MODEL slx_c33119aba72b
CONFIG AbsTol = auto
CONFIG EnableMultiTasking = off
CONFIG FixedStep = auto
CONFIG MaxStep = 1e-3
CONFIG MinStep = auto
CONFIG RelTol = 1e-3
CONFIG SampleTimeConstraint = Unconstrained
CONFIG SolverName = ode15s
CONFIG StartTime = 0.0
CONFIG StopTime = 10
BLOCK [Mux] Mux1
  DisplayOption = bar
  Inputs = 3
BLOCK [Reference] PID Controller  REF=slpidlib/PID Controller
  LibrarySourceBlock = simulink/Continuous/PID Controller
  SourceBlock = slpidlib/PID Controller
  SourceType = PID 1dof
BLOCK [Sin] Pa(t)
  Bias = 0.8
  Frequency = 2*pi*95/60
  SampleTime = 0
BLOCK [SubSystem] Pp(t): Caso [Hipotenso]
BLOCK [Gain] Pp(t): Caso [Hipotenso]/1//L
  Gain = 1/0.005
BLOCK [Gain] Pp(t): Caso [Hipotenso]/1//Z
  Gain = 1/0.02
BLOCK [Sum] Pp(t): Caso [Hipotenso]/Add
  IconShape = rectangular
  Inputs = ++-
BLOCK [Sum] Pp(t): Caso [Hipotenso]/Add1
  IconShape = rectangular
  Inputs = +-
BLOCK [Gain] Pp(t): Caso [Hipotenso]/C
  Gain = 0.250
BLOCK [Derivative] Pp(t): Caso [Hipotenso]/Derivative
BLOCK [Integrator] Pp(t): Caso [Hipotenso]/Integrator
BLOCK [Inport] Pp(t): Caso [Hipotenso]/Pa(t)
BLOCK [Outport] Pp(t): Caso [Hipotenso]/Pp(t)
BLOCK [Gain] Pp(t): Caso [Hipotenso]/RZ//R+Z
  Gain = 0.01935
BLOCK [SubSystem] Pp(t): Control [Normotenso]
BLOCK [Gain] Pp(t): Control [Normotenso]/1//L
  Gain = 1/0.010
BLOCK [Gain] Pp(t): Control [Normotenso]/1//Z
  Gain = 1/0.033
BLOCK [Sum] Pp(t): Control [Normotenso]/Add
  IconShape = rectangular
  Inputs = ++-
BLOCK [Sum] Pp(t): Control [Normotenso]/Add1
  IconShape = rectangular
  Inputs = +-
BLOCK [Gain] Pp(t): Control [Normotenso]/C
  Gain = 1.5
BLOCK [Derivative] Pp(t): Control [Normotenso]/Derivative
BLOCK [Integrator] Pp(t): Control [Normotenso]/Integrator
BLOCK [Inport] Pp(t): Control [Normotenso]/Pa(t)
BLOCK [Outport] Pp(t): Control [Normotenso]/Pp(t)
BLOCK [Gain] Pp(t): Control [Normotenso]/RZ//R+Z
  Gain = 0.0319
BLOCK [SubSystem] Pp(t): Control [Tratamiento]
BLOCK [Gain] Pp(t): Control [Tratamiento]/1//L
  Gain = 1/0.005
BLOCK [Gain] Pp(t): Control [Tratamiento]/1//Z
  Gain = 1/0.020
BLOCK [Sum] Pp(t): Control [Tratamiento]/Add
  IconShape = rectangular
  Inputs = ++-
BLOCK [Sum] Pp(t): Control [Tratamiento]/Add1
  IconShape = rectangular
  Inputs = +-
BLOCK [Gain] Pp(t): Control [Tratamiento]/C
  Gain = 0.250
BLOCK [Derivative] Pp(t): Control [Tratamiento]/Derivative
BLOCK [Integrator] Pp(t): Control [Tratamiento]/Integrator
BLOCK [Inport] Pp(t): Control [Tratamiento]/Pa(t)
BLOCK [Outport] Pp(t): Control [Tratamiento]/Pp(t)
BLOCK [Gain] Pp(t): Control [Tratamiento]/RZ//R+Z
  Gain = 0.01935
BLOCK [Scope] Scope1
  Floating = off
  NumInputPorts = 1
  ScopeSpecificationString = Simulink.scopes.TimeScopeBlockCfg('CurrentConfiguration', extmgr.ConfigurationSet(extmgr.Configuration('Core','General UI',true,'FigureColor',[1 1 1]),extmgr.Configuration('Core','Source UI',true),extmgr.Configuration('Sources','WiredSimulink',true),extmgr.Configuration('Visuals','Time Domain',true,'SerializedDisplays',{struct('MinYLimReal','-0.47294','MaxYLimReal','2.0576','YLabelReal','','MinYLi...<+1846ch>
BLOCK [Sum] Sum
  Inputs = |+-
BLOCK [ToWorkspace] To Workspace
  FixptAsFi = on
  MaxDataPoints = inf
  SampleTime = -1
  SaveFormat = Timeseries
  VariableName = Ppx
BLOCK [ToWorkspace] To Workspace1
  FixptAsFi = on
  MaxDataPoints = inf
  SampleTime = -1
  SaveFormat = Timeseries
  VariableName = Ppy
BLOCK [ToWorkspace] To Workspace3
  FixptAsFi = on
  MaxDataPoints = inf
  SampleTime = -1
  SaveFormat = Timeseries
  VariableName = PA
BLOCK [ToWorkspace] To Workspace4
  FixptAsFi = on
  MaxDataPoints = inf
  SampleTime = -1
  SaveFormat = Timeseries
  VariableName = Ppz
LINE Mux1:1 -> Scope1:1
LINE PID Controller:1 -> Pp(t): Control [Tratamiento]:1
LINE Pa(t):1 -> Pp(t): Caso [Hipotenso]:1
LINE Pa(t):1 -> Pp(t): Control [Normotenso]:1
LINE Pa(t):1 -> To Workspace3:1
LINE Pp(t): Caso [Hipotenso]/1//L:1 -> Pp(t): Caso [Hipotenso]/Integrator:1
LINE Pp(t): Caso [Hipotenso]/1//Z:1 -> Pp(t): Caso [Hipotenso]/Add:1
LINE Pp(t): Caso [Hipotenso]/Add1:1 -> Pp(t): Caso [Hipotenso]/1//L:1
LINE Pp(t): Caso [Hipotenso]/Add:1 -> Pp(t): Caso [Hipotenso]/RZ//R+Z:1
LINE Pp(t): Caso [Hipotenso]/C:1 -> Pp(t): Caso [Hipotenso]/Derivative:1
LINE Pp(t): Caso [Hipotenso]/Derivative:1 -> Pp(t): Caso [Hipotenso]/Add:3
LINE Pp(t): Caso [Hipotenso]/Integrator:1 -> Pp(t): Caso [Hipotenso]/Add:2
LINE Pp(t): Caso [Hipotenso]/Pa(t):1 -> Pp(t): Caso [Hipotenso]/1//Z:1
LINE Pp(t): Caso [Hipotenso]/Pa(t):1 -> Pp(t): Caso [Hipotenso]/Add1:1
LINE Pp(t): Caso [Hipotenso]/RZ//R+Z:1 -> Pp(t): Caso [Hipotenso]/Add1:2
LINE Pp(t): Caso [Hipotenso]/RZ//R+Z:1 -> Pp(t): Caso [Hipotenso]/C:1
LINE Pp(t): Caso [Hipotenso]/RZ//R+Z:1 -> Pp(t): Caso [Hipotenso]/Pp(t):1
LINE Pp(t): Caso [Hipotenso]:1 -> Mux1:3
LINE Pp(t): Caso [Hipotenso]:1 -> To Workspace1:1
LINE Pp(t): Control [Normotenso]/1//L:1 -> Pp(t): Control [Normotenso]/Integrator:1
LINE Pp(t): Control [Normotenso]/1//Z:1 -> Pp(t): Control [Normotenso]/Add:1
LINE Pp(t): Control [Normotenso]/Add1:1 -> Pp(t): Control [Normotenso]/1//L:1
LINE Pp(t): Control [Normotenso]/Add:1 -> Pp(t): Control [Normotenso]/RZ//R+Z:1
LINE Pp(t): Control [Normotenso]/C:1 -> Pp(t): Control [Normotenso]/Derivative:1
LINE Pp(t): Control [Normotenso]/Derivative:1 -> Pp(t): Control [Normotenso]/Add:3
LINE Pp(t): Control [Normotenso]/Integrator:1 -> Pp(t): Control [Normotenso]/Add:2
LINE Pp(t): Control [Normotenso]/Pa(t):1 -> Pp(t): Control [Normotenso]/1//Z:1
LINE Pp(t): Control [Normotenso]/Pa(t):1 -> Pp(t): Control [Normotenso]/Add1:1
LINE Pp(t): Control [Normotenso]/RZ//R+Z:1 -> Pp(t): Control [Normotenso]/Add1:2
LINE Pp(t): Control [Normotenso]/RZ//R+Z:1 -> Pp(t): Control [Normotenso]/C:1
LINE Pp(t): Control [Normotenso]/RZ//R+Z:1 -> Pp(t): Control [Normotenso]/Pp(t):1
LINE Pp(t): Control [Normotenso]:1 -> Mux1:1
LINE Pp(t): Control [Normotenso]:1 -> Sum:1
LINE Pp(t): Control [Normotenso]:1 -> To Workspace:1
LINE Pp(t): Control [Tratamiento]/1//L:1 -> Pp(t): Control [Tratamiento]/Integrator:1
LINE Pp(t): Control [Tratamiento]/1//Z:1 -> Pp(t): Control [Tratamiento]/Add:1
LINE Pp(t): Control [Tratamiento]/Add1:1 -> Pp(t): Control [Tratamiento]/1//L:1
LINE Pp(t): Control [Tratamiento]/Add:1 -> Pp(t): Control [Tratamiento]/RZ//R+Z:1
LINE Pp(t): Control [Tratamiento]/C:1 -> Pp(t): Control [Tratamiento]/Derivative:1
LINE Pp(t): Control [Tratamiento]/Derivative:1 -> Pp(t): Control [Tratamiento]/Add:3
LINE Pp(t): Control [Tratamiento]/Integrator:1 -> Pp(t): Control [Tratamiento]/Add:2
LINE Pp(t): Control [Tratamiento]/Pa(t):1 -> Pp(t): Control [Tratamiento]/1//Z:1
LINE Pp(t): Control [Tratamiento]/Pa(t):1 -> Pp(t): Control [Tratamiento]/Add1:1
LINE Pp(t): Control [Tratamiento]/RZ//R+Z:1 -> Pp(t): Control [Tratamiento]/Add1:2
LINE Pp(t): Control [Tratamiento]/RZ//R+Z:1 -> Pp(t): Control [Tratamiento]/C:1
LINE Pp(t): Control [Tratamiento]/RZ//R+Z:1 -> Pp(t): Control [Tratamiento]/Pp(t):1
LINE Pp(t): Control [Tratamiento]:1 -> Mux1:2
LINE Pp(t): Control [Tratamiento]:1 -> Sum:2
LINE Pp(t): Control [Tratamiento]:1 -> To Workspace4:1
LINE Sum:1 -> PID Controller:1
